# Revit family: 56532203(2020)
name_source: partatom
category: Plumbing Fixtures
units: mm (PartAtom-declared; Revit-internal decimal feet)

## family parameters
Always vertical = Yes
Cut with Voids When Loaded = No
OmniClass Number = 23.45.55.00
OmniClass Title = Sanitary Faucets, Wastes
Part Type = Normal
Room Calculation Point = No
Round Connector Dimension = Use Diameter
Shared = No
Work Plane-Based = No

## types (1)
- 56532203 Kitchen faucet
    2D/3D/BIM Files URL = http://static.hansa.com
    3D View = https://static.hansa.com
    Advanced Features = Inner body made of DZR brass;3S-installation system for safe and simple mounting
    Aerator = Standard aerator
    Ambience photo = http://static.hansa.com
    Approval ABP = P-IX 38252/IA
    Approval DVGW = DW-6506CS0548
    AssetType = Fixed
    BIMObjectName = 56532203(2020)
    Backflow Prevention EN1717 = AA
    BodyMaterial = Brass
    Brand = HANSA
    CO2 Emissions (A1-A3) = 11.94
    CO2 Emissions (A4) = 0.24
    CO2 Emissions (B7) = 4728
    CO2 Emissions (C2) = 0.02
    CO2 Emissions (C3) = 0.02
    CO2 Emissions (C4) = 0.36
    CO2 Emissions (D) = -6.75
    Catalog Drawing URL = http://static.hansa.com
    Category = Kitchen
    CloseOffRating = 0
    Color = Chrome
    Connection = Flexible inlet pipes
    Connection Size = G3/8
    Default Elevation = 0 mm  [stored 0 ft]
    Dimension Drawing URL = http://static.hansa.com
    DurationUnit = Year
    EAN Number = 4057304012297
    EN Standard = EN 817
    ETIM Class Number = EC011431 Kitchen mixing tap
    FDV Document URL = http://www.hansa.com
    FaucetMainMaterial = Brass
    Features = Single-lever
    Finish = Polished
    Flow Drawing URL = http://static.hansa.com
    Flow Rate At 300kPa = 0.2 L/s
    FlowCoefficient = 0
    Group = Kitchen faucet
    IfcExportAs = IfcValveType
    IfcExportType = FAUCET
    InletConnectionSize = 10 mm  [stored 0.0328084 ft]
    Installation Type = Deck mounted
    Installation and Maintenance Guide URL = http://static.hansa.com
    Interactive AR View URL = https://static.hansa.com
    Lever Handle = Hot/Cold symbols;Single operating lever/handle
    Manufacturer = HANSA
    ManufacturerName = HANSA
    ManufacturerURL = http://www.hansa.com
    Market = International;Germany;Austria;Switzerland;France;Italy;Spain
    Material = Brass
    Max. Hot Water Supply = 70 °C
    Mechanical Parts = ø 35 mm ceramic cartridge for flow and temperature control
    Mobile Product Information URL = http://mpi.hansa.com
    Model = 56532203 Kitchen faucet
    ModelReference = 56532203
    Mounting Holes = 1 hole
    NBSDescription = Water supply fittings for wash basins and troughs
    NBSReference = 45-35-70/371
    Name = 56532203 Kitchen faucet
    Name_en = 56532203 Kitchen faucet
    Noise Class = I (ISO 3822)
    NominalDepth = 255 mm
    NominalHeight = 169 mm
    NominalWidth = 51 mm
    Product Code = 56532203
    Product Family = HANSAPALENO
    Product Image URL = http://static.hansa.com
    Product URL = http://static.hansa.com
    Sales Package dimensions (LxWxH) = 362 x 278 x 63
    Shape = Sculptured
    Size = 50x255x170 mm
    Spare-Part Information URL = http://static.hansa.com
    Spout Projection = 216 mm
    Spout Swivel Range = 120°
    Spout Type = Swivel spout;Swivel range limiting option
    Surface treatment = Chrome
    Technical DataSheet URL = http://www.hansa.com
    Temperature = Temperature limiter;Temperature limiter (retrofittable)
    Temperature Adjustments = Limitation option for maximum temperature and flow-rate ;Adjustable hot water stop (included, retrofittable)
    UNSPSC Class Number = 30181700 Faucets or taps
    URL ABP = http://static.hansa.com
    URL DVGW = http://static.hansa.com
    URL Declaration Of Performance (DOP) = http://static.hansa.com
    URL Declaration of Asbestos = http://static.hansa.com
    URL Declaration of Conformity = http://static.hansa.com
    URL Declaration of SCIP = http://static.hansa.com
    URL EU Packaging Declaration = http://static.hansa.com
    URL EcoLabel Declaration = http://static.hansa.com
    URL Environmental Product Declaration EPD = http://www.hansa.com faucet.pdf
    URL Materials Declaration = http://www.hansa.com
    URL REACH = http://static.hansa.com
    Uniclass2 = Pr_40_30_96_96
    Uniclass2015Description = Washbasin manual water supply sets
    Uniclass2015Reference = Pr_40_20_87_96
    Version = 1
    VersionDate = 01/06/2023
    Warranty Information URL = http://warranty.hansa.com
    WarrantyDescription = http://warranty.hansa.com
    WarrantyDurationUnit = Year
    Working Pressure = 50 - 1000 kPa

note: [stored X ft] marks values corroborated as IEEE doubles in the binary element streams (Revit-internal decimal feet)

## geometry (parser evidence)
native form markers: Sweep x4
no freeform markers — native parametric forms only
